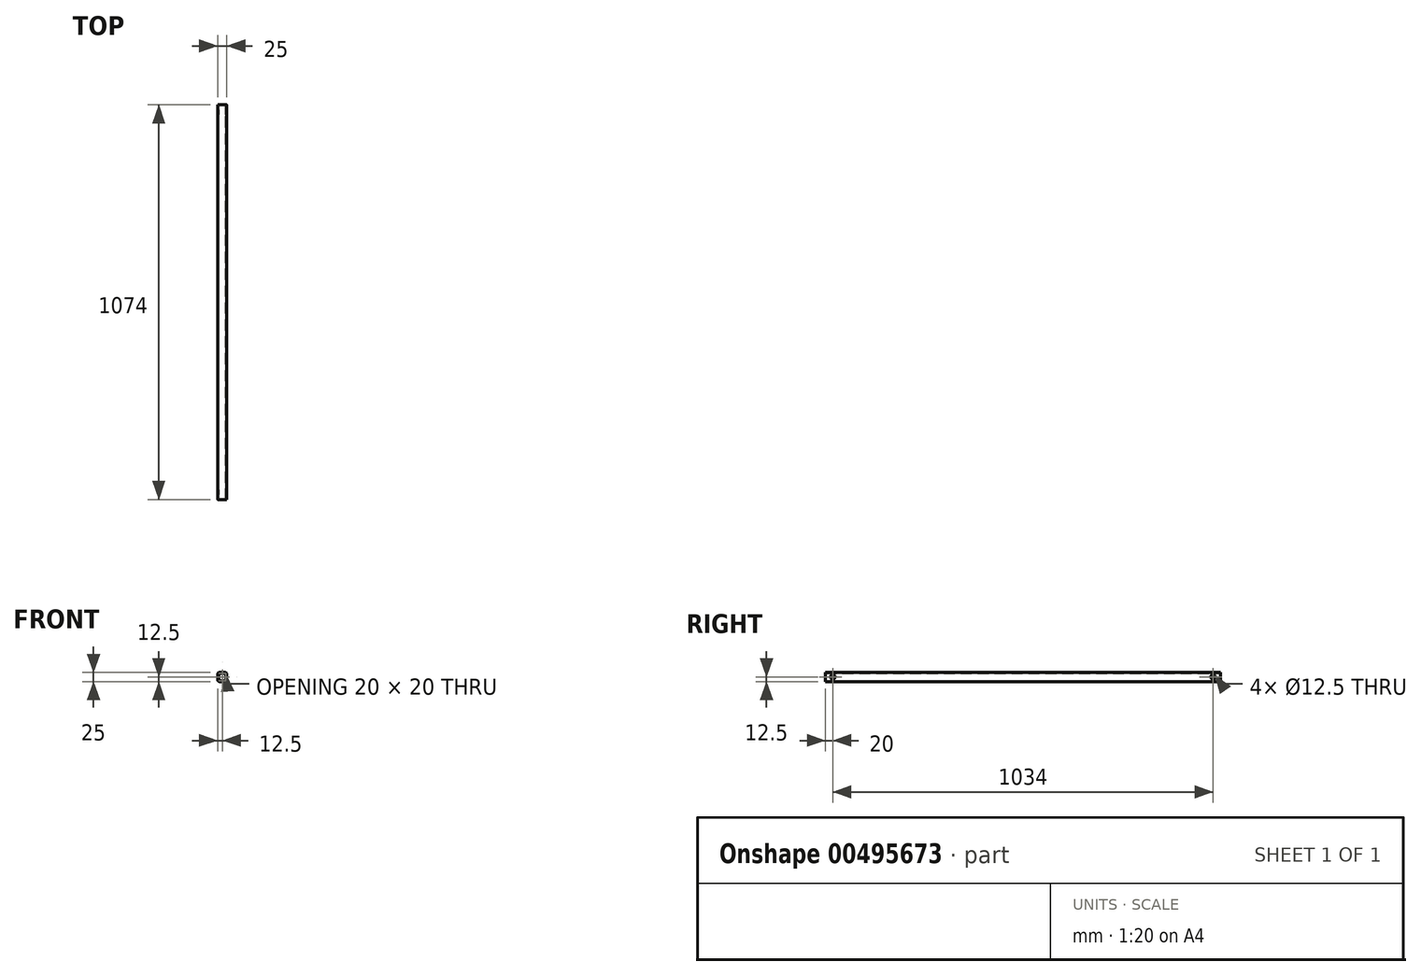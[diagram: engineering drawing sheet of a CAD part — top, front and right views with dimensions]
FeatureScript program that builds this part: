
annotation { "Feature Type Name" : "Feature", "Feature Type Description" : "" }
export const myFeature = defineFeature(function(context is Context, id is Id, definition is map)
    precondition{}
    {
        {
            var Q0;
            Q0=qCreatedBy(makeId("Front.planeOp"),FACE);
            var sketch = newSketch(context, id + "F0", { "sketchPlane" : qUnion([Q0])});
            skLineSegment(sketch, "E0.bottom", {"start": v(7.5, 12.5) * mm, "end": v(-7.5, 12.5) * mm});
            skLineSegment(sketch, "E0.top", {"start": v(7.5, -12.5) * mm, "end": v(-7.5, -12.5) * mm});
            skLineSegment(sketch, "E0.left", {"start": v(12.5, 7.5) * mm, "end": v(12.5, -7.5) * mm});
            skLineSegment(sketch, "E0.right", {"start": v(-12.5, 7.5) * mm, "end": v(-12.5, -7.5) * mm});
            skPoint(sketch, "E0.middle", {"position": v(0, 0) * mm});
            skPoint(sketch, "E1.visualSharp", {"position": v(-12.5, 12.5) * mm});
            skArc(sketch, "E1.filletArc", {"start": v(-7.5, 12.5) * mm, "mid": v(-11.04, 11.04) * mm, "end": v(-12.5, 7.5) * mm});
            skPoint(sketch, "E2.visualSharp", {"position": v(12.5, 12.5) * mm});
            skArc(sketch, "E2.filletArc", {"start": v(12.5, 7.5) * mm, "mid": v(11.04, 11.04) * mm, "end": v(7.5, 12.5) * mm});
            skPoint(sketch, "E3.visualSharp", {"position": v(12.5, -12.5) * mm});
            skArc(sketch, "E3.filletArc", {"start": v(7.5, -12.5) * mm, "mid": v(11.04, -11.04) * mm, "end": v(12.5, -7.5) * mm});
            skPoint(sketch, "E4.visualSharp", {"position": v(-12.5, -12.5) * mm});
            skArc(sketch, "E4.filletArc", {"start": v(-12.5, -7.5) * mm, "mid": v(-11.04, -11.04) * mm, "end": v(-7.5, -12.5) * mm});
            skLineSegment(sketch, "E5.0", {"start": v(7.5, 10) * mm, "end": v(-7.5, 10) * mm});
            skArc(sketch, "E5.1", {"start": v(10, 7.5) * mm, "mid": v(9.27, 9.27) * mm, "end": v(7.5, 10) * mm});
            skArc(sketch, "E5.2", {"start": v(-7.5, 10) * mm, "mid": v(-9.27, 9.27) * mm, "end": v(-10, 7.5) * mm});
            skLineSegment(sketch, "E5.3", {"start": v(10, 7.5) * mm, "end": v(10, -7.5) * mm});
            skLineSegment(sketch, "E5.4", {"start": v(-10, 7.5) * mm, "end": v(-10, -7.5) * mm});
            skArc(sketch, "E5.5", {"start": v(-10, -7.5) * mm, "mid": v(-9.27, -9.27) * mm, "end": v(-7.5, -10) * mm});
            skLineSegment(sketch, "E5.6", {"start": v(7.5, -10) * mm, "end": v(-7.5, -10) * mm});
            skArc(sketch, "E5.7", {"start": v(7.5, -10) * mm, "mid": v(9.27, -9.27) * mm, "end": v(10, -7.5) * mm});
            skSolve(sketch);
        }
        {
            var Q0;
            Q0=qSketchRegion(id+"F0",true);
            extrude(context, id + "F1", {"entities" : qUnion([Q0]), "endBound" : BoundingType.SYMMETRIC, "depth" : 1074 * mm});
        }
        {
            var Q0;
            Q0=makeQuery(id+"F1.opExtrude","SWEPT_FACE",FACE,{"disambiguationData":[OSD([sQuery(id+"F0.wireOp",EDGE,"E0.left")])]});
            var sketch = newSketch(context, id + "F2", { "sketchPlane" : qUnion([Q0])});
            skLineSegment(sketch, "E6", {"start": v(-537, 0) * mm, "end": v(-517, 0) * mm, "construction": true});
            skCircle(sketch, "E7", {"center": v(-517, 0) * mm, "radius": 6.25 * mm});
            skLineSegment(sketch, "E8", {"start": v(0, 0) * mm, "end": v(0, 13.57) * mm, "construction": true});
            skPoint(sketch, "E8.endSnap0", {"position": v(0, 7.5) * mm});
            skCircle(sketch, "E9.MirrorC", {"center": v(517, 0) * mm, "radius": 6.25 * mm});
            skSolve(sketch);
        }
        {
            var Q0;
            Q0=qSketchRegion(id+"F2",true);
            extrude(context, id + "F3", {"entities" : qUnion([Q0]), "operationType" : NewBodyOperationType.REMOVE, "endBound" : BoundingType.THROUGH_ALL, "oppositeDirection" : true, "depth" : 25 * mm});
        }
    });
